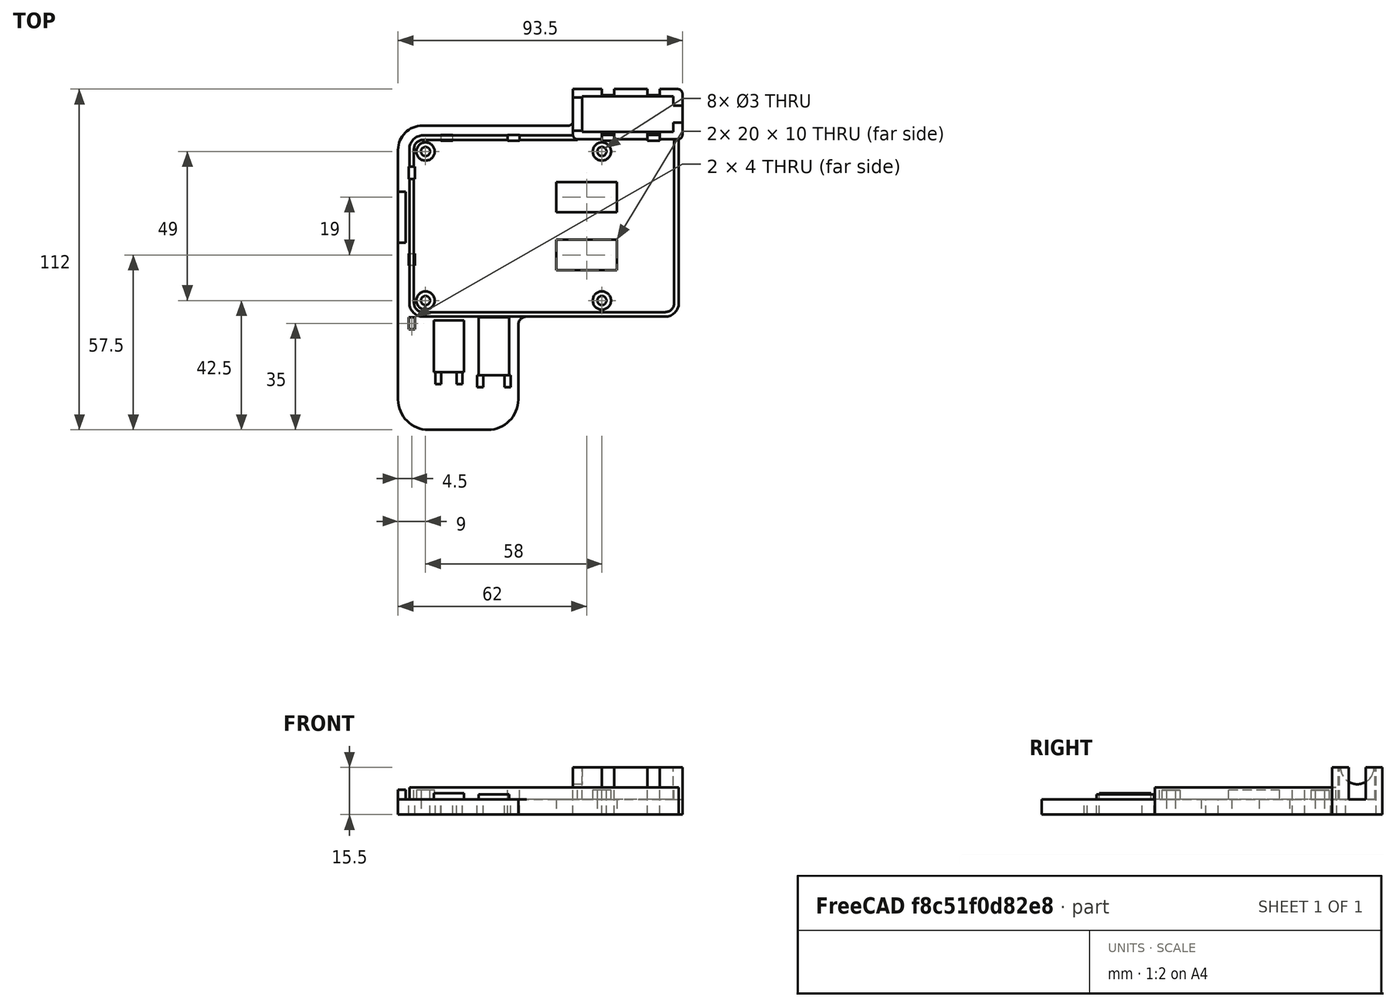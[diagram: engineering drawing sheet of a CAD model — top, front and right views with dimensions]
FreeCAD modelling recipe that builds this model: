
FCSTD DOCUMENT  (FreeCAD 0.18R4 (GitTag))
Label: v1.1raspberry_holster
License: All rights reserved
LicenseURL: http://en.wikipedia.org/wiki/All_rights_reserved
objects: Sketcher::SketchObject×10, PartDesign::Pad×7, PartDesign::Pocket×3, Mesh::Feature×1, PartDesign::Body×1
note: 31 computed .brp shape members not serialized (recipe doc carries the construction recipe); baked Part::Feature solids carry a one-line shape summary decoded from their .brp

FEATURE [Mesh::Feature] Raspberry_Pi_4
  Placement = pos=(39,24.5,7.5) rot=(0,0,1;0rad)
FEATURE [Sketcher::SketchObject] Sketch  label="bottom_plane"
  MapMode = 5
  Support = -> [XY_Plane]
  sketch-geometry (71):
    g0: Circle CenterX=0 CenterY=49 CenterZ=0 NormalX=0 NormalY=0 NormalZ=1 AngleXU=0 Radius=1.5
    g1: Circle CenterX=58 CenterY=49 CenterZ=0 NormalX=0 NormalY=0 NormalZ=1 AngleXU=0 Radius=1.5
    g2: Circle CenterX=0 CenterY=0 CenterZ=0 NormalX=0 NormalY=0 NormalZ=1 AngleXU=0 Radius=1.5
    g3: Circle CenterX=58 CenterY=0 CenterZ=0 NormalX=0 NormalY=0 NormalZ=1 AngleXU=0 Radius=1.5
    g4: LineSegment StartX=84.5 StartY=68 StartZ=0 EndX=84.5 EndY=-5 EndZ=0
    g5: ArcOfCircle CenterX=83 CenterY=68 CenterZ=0 NormalX=0 NormalY=0 NormalZ=1 AngleXU=0 Radius=1.5 StartAngle=-9e-16 EndAngle=1.5708
    g6: LineSegment StartX=48.5 StartY=69.5 StartZ=0 EndX=48.5 EndY=59 EndZ=0
    g7: ArcOfCircle CenterX=47 CenterY=59 CenterZ=0 NormalX=0 NormalY=0 NormalZ=1 AngleXU=0 Radius=1.5 StartAngle=4.71239 EndAngle=6.28319
    g8: LineSegment StartX=47 StartY=57.5 StartZ=0 EndX=-1 EndY=57.5 EndZ=0
    g9: LineSegment StartX=-9 StartY=49.5 StartZ=0 EndX=-9 EndY=-32.5 EndZ=0
    g10: ArcOfCircle CenterX=-1 CenterY=49.5 CenterZ=0 NormalX=0 NormalY=0 NormalZ=1 AngleXU=0 Radius=8 StartAngle=1.5708 EndAngle=3.14159
    g11: LineSegment StartX=1 StartY=-42.5 StartZ=0 EndX=20.5 EndY=-42.5 EndZ=0
    g12: ArcOfCircle CenterX=1 CenterY=-32.5 CenterZ=0 NormalX=0 NormalY=0 NormalZ=1 AngleXU=0 Radius=10 StartAngle=3.14159 EndAngle=4.71239
    g13: ArcOfCircle CenterX=83 CenterY=-5 CenterZ=0 NormalX=0 NormalY=0 NormalZ=1 AngleXU=0 Radius=1.5 StartAngle=4.71239 EndAngle=6.28319
    g14: LineSegment StartX=32 StartY=-6.5 StartZ=0 EndX=83 EndY=-6.5 EndZ=0
    g15: LineSegment StartX=30.5 StartY=-8 StartZ=0 EndX=30.5 EndY=-32.5 EndZ=0
    g16: ArcOfCircle CenterX=32 CenterY=-8 CenterZ=0 NormalX=0 NormalY=0 NormalZ=1 AngleXU=0 Radius=1.5 StartAngle=1.5708 EndAngle=3.14159
    g17: ArcOfCircle CenterX=20.5 CenterY=-32.5 CenterZ=0 NormalX=0 NormalY=0 NormalZ=1 AngleXU=0 Radius=10 StartAngle=4.71239 EndAngle=6.28319
    g18: LineSegment StartX=58 StartY=52.5 StartZ=0 EndX=62 EndY=52.5 EndZ=0
    g19: LineSegment StartX=62 StartY=52.5 StartZ=0 EndX=62 EndY=54.5 EndZ=0
    g20: LineSegment StartX=62 StartY=54.5 StartZ=0 EndX=58 EndY=54.5 EndZ=0
    g21: LineSegment StartX=58 StartY=54.5 StartZ=0 EndX=58 EndY=52.5 EndZ=0
    g22: LineSegment StartX=73 StartY=54.5 StartZ=0 EndX=77 EndY=54.5 EndZ=0
    g23: LineSegment StartX=77 StartY=54.5 StartZ=0 EndX=77 EndY=52.5 EndZ=0
    g24: LineSegment StartX=77 StartY=52.5 StartZ=0 EndX=73 EndY=52.5 EndZ=0
    g25: LineSegment StartX=73 StartY=52.5 StartZ=0 EndX=73 EndY=54.5 EndZ=0
    g26: LineSegment StartX=48.5 StartY=69.5 StartZ=0 EndX=58 EndY=69.5 EndZ=0
    g27: LineSegment StartX=58 StartY=69.5 StartZ=0 EndX=58 EndY=67.5 EndZ=0
    g28: LineSegment StartX=58 StartY=67.5 StartZ=0 EndX=62 EndY=67.5 EndZ=0
    g29: LineSegment StartX=62 StartY=67.5 StartZ=0 EndX=62 EndY=69.5 EndZ=0
    g30: LineSegment StartX=62 StartY=69.5 StartZ=0 EndX=73 EndY=69.5 EndZ=0
    g31: LineSegment StartX=73 StartY=69.5 StartZ=0 EndX=73 EndY=67.5 EndZ=0
    g32: LineSegment StartX=73 StartY=67.5 StartZ=0 EndX=77 EndY=67.5 EndZ=0
    g33: LineSegment StartX=77 StartY=67.5 StartZ=0 EndX=77 EndY=69.5 EndZ=0
    g34: LineSegment StartX=77 StartY=69.5 StartZ=0 EndX=83 EndY=69.5 EndZ=0
    g35: LineSegment StartX=31 StartY=54.5 StartZ=0 EndX=27 EndY=54.5 EndZ=0
    g36: LineSegment StartX=27 StartY=54.5 StartZ=0 EndX=27 EndY=52.5 EndZ=0
    g37: LineSegment StartX=27 StartY=52.5 StartZ=0 EndX=31 EndY=52.5 EndZ=0
    g38: LineSegment StartX=31 StartY=52.5 StartZ=0 EndX=31 EndY=54.5 EndZ=0
    g39: LineSegment StartX=9 StartY=54.5 StartZ=0 EndX=5 EndY=54.5 EndZ=0
    g40: LineSegment StartX=5 StartY=54.5 StartZ=0 EndX=5 EndY=52.5 EndZ=0
    g41: LineSegment StartX=5 StartY=52.5 StartZ=0 EndX=9 EndY=52.5 EndZ=0
    g42: LineSegment StartX=9 StartY=52.5 StartZ=0 EndX=9 EndY=54.5 EndZ=0
    g43: LineSegment StartX=-5.5 StartY=44 StartZ=0 EndX=-3.5 EndY=44 EndZ=0
    g44: LineSegment StartX=-3.5 StartY=44 StartZ=0 EndX=-3.5 EndY=40 EndZ=0
    g45: LineSegment StartX=-3.5 StartY=40 StartZ=0 EndX=-5.5 EndY=40 EndZ=0
    g46: LineSegment StartX=-5.5 StartY=40 StartZ=0 EndX=-5.5 EndY=44 EndZ=0
    g47: LineSegment StartX=-5.5 StartY=15.5 StartZ=0 EndX=-3.5 EndY=15.5 EndZ=0
    g48: LineSegment StartX=-3.5 StartY=15.5 StartZ=0 EndX=-3.5 EndY=11.5 EndZ=0
    g49: LineSegment StartX=-3.5 StartY=11.5 StartZ=0 EndX=-5.5 EndY=11.5 EndZ=0
    g50: LineSegment StartX=-5.5 StartY=11.5 StartZ=0 EndX=-5.5 EndY=15.5 EndZ=0
    g51: LineSegment StartX=-5.5 StartY=-5.5 StartZ=0 EndX=-3.5 EndY=-5.5 EndZ=0
    g52: LineSegment StartX=-3.5 StartY=-5.5 StartZ=0 EndX=-3.5 EndY=-9.5 EndZ=0
    g53: LineSegment StartX=-3.5 StartY=-9.5 StartZ=0 EndX=-5.5 EndY=-9.5 EndZ=0
    g54: LineSegment StartX=-5.5 StartY=-9.5 StartZ=0 EndX=-5.5 EndY=-5.5 EndZ=0
    g55: LineSegment StartX=3.2 StartY=-23.5 StartZ=0 EndX=5.2 EndY=-23.5 EndZ=0
    g56: LineSegment StartX=5.2 StartY=-23.5 StartZ=0 EndX=5.2 EndY=-27.5 EndZ=0
    g57: LineSegment StartX=5.2 StartY=-27.5 StartZ=0 EndX=3.2 EndY=-27.5 EndZ=0
    g58: LineSegment StartX=3.2 StartY=-27.5 StartZ=0 EndX=3.2 EndY=-23.5 EndZ=0
    g59: LineSegment StartX=10.2 StartY=-23.5 StartZ=0 EndX=12.2 EndY=-23.5 EndZ=0
    g60: LineSegment StartX=12.2 StartY=-23.5 StartZ=0 EndX=12.2 EndY=-27.5 EndZ=0
    g61: LineSegment StartX=12.2 StartY=-27.5 StartZ=0 EndX=10.2 EndY=-27.5 EndZ=0
    g62: LineSegment StartX=10.2 StartY=-27.5 StartZ=0 EndX=10.2 EndY=-23.5 EndZ=0
    g63: LineSegment StartX=17 StartY=-24.5 StartZ=0 EndX=19 EndY=-24.5 EndZ=0
    g64: LineSegment StartX=19 StartY=-24.5 StartZ=0 EndX=19 EndY=-28.5 EndZ=0
    g65: LineSegment StartX=19 StartY=-28.5 StartZ=0 EndX=17 EndY=-28.5 EndZ=0
    g66: LineSegment StartX=17 StartY=-28.5 StartZ=0 EndX=17 EndY=-24.5 EndZ=0
    g67: LineSegment StartX=26 StartY=-24.5 StartZ=0 EndX=28 EndY=-24.5 EndZ=0
    g68: LineSegment StartX=28 StartY=-24.5 StartZ=0 EndX=28 EndY=-28.5 EndZ=0
    g69: LineSegment StartX=28 StartY=-28.5 StartZ=0 EndX=26 EndY=-28.5 EndZ=0
    g70: LineSegment StartX=26 StartY=-28.5 StartZ=0 EndX=26 EndY=-24.5 EndZ=0
  constraints (219):
    c: Coincident(g-1,g2)
    c: Vertical(g2,g0)
    c: Vertical(g1,g3)
    c: Horizontal(g1,g0)
    c: Horizontal(g3,g2)
    c: DistanceY(g2,g0) = 49
    c: DistanceX(g2,g3) = 58
    c: Radius(g2) = 1.5
    c: Equal(g2,g3)
    c: Equal(g3,g1)
    c: Equal(g1,g0)
    c: Vertical(g4)
    c: DistanceX(g3,g4) = 26.5
    c: Coincident(g5,g4)
    c: Vertical(g5,g5)
    c: Horizontal(g4,g5)
    c: Radius(g5) = 1.5
    c: Coincident(g6,g7)
    c: Vertical(g7,g7)
    c: Horizontal(g7,g6)
    c: Radius(g7) = 1.5
    c: Vertical(g6)
    c: DistanceX(g6,g4) = 36
    c: Coincident(g8,g7)
    c: Horizontal(g8)
    c: Vertical(g9)
    c: DistanceX(g9,g0) = 9
    c: DistanceY(g1,g7) = 8.5
    c: Coincident(g10,g8)
    c: Coincident(g9,g10)
    c: Vertical(g10,g8)
    c: Horizontal(g10,g9)
    c: Horizontal(g11)
    c: DistanceY(g11,g2) = 42.5
    c: Coincident(g11,g12)
    c: Coincident(g12,g9)
    c: Vertical(g12,g11)
    c: Horizontal(g9,g12)
    c: Coincident(g13,g4)
    c: Horizontal(g13,g4)
    c: Vertical(g13,g13)
    c: Radius(g13) = 1.5
    c: Coincident(g14,g13)
    c: Horizontal(g14)
    c: Coincident(g16,g14)
    c: Coincident(g16,g15)
    c: Vertical(g16,g14)
    c: Horizontal(g16,g15)
    c: DistanceY(g14,g3) = 6.5
    c: DistanceX(g2,g15) = 30.5
    c: Vertical(g15)
    c: Coincident(g17,g11)
    c: Coincident(g17,g15)
    c: Horizontal(g17,g15)
    c: Vertical(g11,g17)
    c: Radius(g16) = 1.5
    c: Coincident(g18,g19)
    c: Coincident(g19,g20)
    c: Coincident(g20,g21)
    c: Coincident(g21,g18)
    c: Horizontal(g18)
    c: Horizontal(g20)
    c: Vertical(g19)
    c: Vertical(g21)
    c: DistanceY(g18,g20) = 2
    c: DistanceX(g20,g19) = 4
    c: DistanceY(g1,g18) = 3.5
    c: Vertical(g1,g18)
    c: Coincident(g22,g23)
    c: Coincident(g23,g24)
    c: Coincident(g24,g25)
    c: Coincident(g25,g22)
    c: Horizontal(g22)
    c: Horizontal(g24)
    c: Vertical(g23)
    c: Vertical(g25)
    c: Horizontal(g22,g19)
    c: Horizontal(g24,g18)
    c: DistanceX(g22,g22) = 4
    c: DistanceX(g18,g24) = 15
    c: Coincident(g26,g27)
    c: Coincident(g27,g28)
    c: Coincident(g28,g29)
    c: Coincident(g29,g30)
    c: Coincident(g30,g31)
    c: Coincident(g31,g32)
    c: Coincident(g32,g33)
    c: Coincident(g33,g34)
    c: Coincident(g26,g6)
    c: Coincident(g34,g5)
    c: DistanceY(g1,g6) = 20.5
    c: Horizontal(g26)
    c: Horizontal(g30)
    c: Horizontal(g32)
    c: Horizontal(g34)
    c: Horizontal(g28)
    c: Vertical(g27)
    c: Vertical(g29)
    c: Vertical(g31)
    c: Vertical(g33)
    c: Horizontal(g26,g29)
    c: Horizontal(g30,g33)
    c: Horizontal(g31,g28)
    c: Vertical(g28,g19)
    c: Vertical(g20,g27)
    c: Vertical(g22,g31)
    c: Vertical(g22,g32)
    c: DistanceY(g28,g29) = 2
    c: Coincident(g35,g36)
    c: Coincident(g36,g37)
    c: Coincident(g38,g35)
    c: Horizontal(g35)
    c: Horizontal(g37)
    c: Vertical(g36)
    c: Vertical(g38)
    c: Coincident(g39,g40)
    c: Coincident(g40,g41)
    c: Coincident(g41,g42)
    c: Coincident(g42,g39)
    c: Horizontal(g39)
    c: Horizontal(g41)
    c: Vertical(g40)
    c: Vertical(g42)
    c: Coincident(g43,g44)
    c: Coincident(g44,g45)
    c: Coincident(g45,g46)
    c: Coincident(g46,g43)
    c: Horizontal(g43)
    c: Horizontal(g45)
    c: Vertical(g44)
    c: Vertical(g46)
    c: Coincident(g47,g48)
    c: Coincident(g48,g49)
    c: Coincident(g49,g50)
    c: Coincident(g50,g47)
    c: Horizontal(g47)
    c: Horizontal(g49)
    c: Vertical(g48)
    c: Vertical(g50)
    c: DistanceY(g1,g37) = 3.5
    c: DistanceX(g36,g37) = 4
    c: DistanceY(g37,g35) = 2
    c: DistanceX(g40,g41) = 4
    c: Horizontal(g41,g36)
    c: Horizontal(g39,g35)
    c: DistanceX(g37,g1) = 27
    c: DistanceX(g43,g0) = 3.5
    c: DistanceX(g43,g43) = 2
    c: DistanceY(g44,g43) = 4
    c: Vertical(g44,g47)
    c: Vertical(g47,g45)
    c: DistanceY(g49,g47) = 4
    c: DistanceY(g43,g0) = 5
    c: DistanceX(g0,g40) = 5
    c: DistanceY(g47,g44) = 24.5
    c: Coincident(g37,g38)
    c: Coincident(g51,g52)
    c: Coincident(g52,g53)
    c: Coincident(g53,g54)
    c: Coincident(g54,g51)
    c: Horizontal(g51)
    c: Horizontal(g53)
    c: Vertical(g52)
    c: Vertical(g54)
    c: Vertical(g51,g49)
    c: Vertical(g51,g48)
    c: DistanceY(g53,g51) = 4
    c: DistanceY(g51,g48) = 17
    c: Coincident(g55,g56)
    c: Coincident(g56,g57)
    c: Coincident(g57,g58)
    c: Coincident(g58,g55)
    c: Horizontal(g55)
    c: Horizontal(g57)
    c: Vertical(g56)
    c: Vertical(g58)
    c: Coincident(g59,g60)
    c: Coincident(g60,g61)
    c: Coincident(g61,g62)
    c: Coincident(g62,g59)
    c: Horizontal(g59)
    c: Horizontal(g61)
    c: Vertical(g60)
    c: Vertical(g62)
    c: Coincident(g63,g64)
    c: Coincident(g64,g65)
    c: Coincident(g65,g66)
    c: Coincident(g66,g63)
    c: Horizontal(g63)
    c: Horizontal(g65)
    c: Vertical(g64)
    c: Vertical(g66)
    c: Coincident(g67,g68)
    c: Coincident(g68,g69)
    c: Coincident(g69,g70)
    c: Coincident(g70,g67)
    c: Horizontal(g67)
    c: Horizontal(g69)
    c: Vertical(g68)
    c: Vertical(g70)
    c: DistanceX(g55,g55) = 2
    c: DistanceY(g56,g55) = 4
    c: Horizontal(g56,g61)
    c: Horizontal(g65,g69)
    c: Horizontal(g67,g63)
    c: Horizontal(g59,g55)
    c: DistanceX(g59,g59) = 2
    c: DistanceX(g63,g63) = 2
    c: DistanceX(g67,g67) = 2
    c: DistanceX(g56,g61) = 5
    c: DistanceX(g64,g69) = 7
    c: DistanceY(g65,g63) = 4
    c: DistanceY(g55,g2) = 23.5
    c: DistanceY(g63,g2) = 24.5
    c: DistanceX(g2,g55) = 5.2
    c: DistanceX(g2,g63) = 19
    c: Radius(g10) = 8
    c: Equal(g12,g17)
    c: Radius(g17) = 10
FEATURE [PartDesign::Pad] Pad  label="bottom_plane_pad"
  Length = 5
  Length2 = 100
  Profile = -> Sketch
  Type = 0
FEATURE [Sketcher::SketchObject] Sketch001  label="standoffs"
  ExternalGeometry = -> [Pad]
  MapMode = 5
  Placement = pos=(0,0,5) rot=(0,0,1;0rad)
  Support = -> [Pad]
  sketch-geometry (8):
    g0: Circle CenterX=0 CenterY=49 CenterZ=0 NormalX=0 NormalY=0 NormalZ=1 AngleXU=0 Radius=3
    g1: Circle CenterX=58 CenterY=49 CenterZ=0 NormalX=0 NormalY=0 NormalZ=1 AngleXU=0 Radius=3
    g2: Circle CenterX=58 CenterY=0 CenterZ=0 NormalX=0 NormalY=0 NormalZ=1 AngleXU=0 Radius=3
    g3: Circle CenterX=0 CenterY=0 CenterZ=0 NormalX=0 NormalY=0 NormalZ=1 AngleXU=0 Radius=3
    g4: Circle CenterX=58 CenterY=0 CenterZ=0 NormalX=0 NormalY=0 NormalZ=1 AngleXU=0 Radius=1.5
    g5: Circle CenterX=58 CenterY=49 CenterZ=0 NormalX=0 NormalY=0 NormalZ=1 AngleXU=0 Radius=1.5
    g6: Circle CenterX=0 CenterY=49 CenterZ=0 NormalX=0 NormalY=0 NormalZ=1 AngleXU=0 Radius=1.5
    g7: Circle CenterX=0 CenterY=0 CenterZ=0 NormalX=0 NormalY=0 NormalZ=1 AngleXU=0 Radius=1.5
  constraints (16):
    c: Coincident(g3,g-1)
    c: Coincident(g-5,g0)
    c: Coincident(g-6,g1)
    c: Coincident(g-3,g2)
    c: Equal(g2,g1)
    c: Equal(g1,g0)
    c: Equal(g0,g3)
    c: Radius(g1) = 3
    c: Coincident(g7,g3)
    c: Coincident(g2,g4)
    c: Coincident(g5,g1)
    c: Coincident(g6,g0)
    c: Equal(g5,g4)
    c: Equal(g4,g7)
    c: Equal(g7,g6)
    c: Equal(g6,g-5)
FEATURE [PartDesign::Pad] Pad001  label="standoffs_pad"
  BaseFeature = -> Pad
  Length = 3
  Length2 = 100
  Profile = -> Sketch001
  Type = 0
FEATURE [Sketcher::SketchObject] Sketch002  label="HDMI_holder"
  ExternalGeometry = -> [Pad001]
  MapMode = 5
  Placement = pos=(0,0,5) rot=(0,0,1;0rad)
  Support = -> [Pad001]
  sketch-geometry (31):
    g0: LineSegment StartX=84.5 StartY=54.5 StartZ=0 EndX=84.5 EndY=58.5 EndZ=0
    g1: LineSegment StartX=51.5 StartY=55.5 StartZ=0 EndX=81.5 EndY=55.5 EndZ=0
    g2: LineSegment StartX=81.5 StartY=55.5 StartZ=0 EndX=81.5 EndY=58.5 EndZ=0
    g3: LineSegment StartX=81.5 StartY=58.5 StartZ=0 EndX=84.5 EndY=58.5 EndZ=0
    g4: LineSegment StartX=51.5 StartY=55.5 StartZ=0 EndX=51.5 EndY=67.1 EndZ=0
    g5: LineSegment StartX=48.5 StartY=69.5 StartZ=0 EndX=48.5 EndY=54.5 EndZ=0
    g6: LineSegment StartX=51.5 StartY=67.1 StartZ=0 EndX=81.5 EndY=67.1 EndZ=0
    g7: LineSegment StartX=81.5 StartY=67.1 StartZ=0 EndX=81.5 EndY=64.1 EndZ=0
    g8: LineSegment StartX=81.5 StartY=64.1 StartZ=0 EndX=84.5 EndY=64.1 EndZ=0
    g9: LineSegment StartX=84.5 StartY=64.1 StartZ=0 EndX=84.5 EndY=68 EndZ=0
    g10: ArcOfCircle CenterX=83 CenterY=68 CenterZ=0 NormalX=0 NormalY=0 NormalZ=1 AngleXU=0 Radius=1.5 StartAngle=1.4e-15 EndAngle=1.5708
    g11: LineSegment StartX=83 StartY=69.5 StartZ=0 EndX=77 EndY=69.5 EndZ=0
    g12: LineSegment StartX=77 StartY=69.5 StartZ=0 EndX=77 EndY=67.5 EndZ=0
    g13: LineSegment StartX=77 StartY=67.5 StartZ=0 EndX=73 EndY=67.5 EndZ=0
    g14: LineSegment StartX=73 StartY=67.5 StartZ=0 EndX=73 EndY=69.5 EndZ=0
    g15: LineSegment StartX=73 StartY=69.5 StartZ=0 EndX=62 EndY=69.5 EndZ=0
    g16: LineSegment StartX=62 StartY=69.5 StartZ=0 EndX=62 EndY=67.5 EndZ=0
    g17: LineSegment StartX=62 StartY=67.5 StartZ=0 EndX=58 EndY=67.5 EndZ=0
    g18: LineSegment StartX=58 StartY=67.5 StartZ=0 EndX=58 EndY=69.5 EndZ=0
    g19: LineSegment StartX=58 StartY=69.5 StartZ=0 EndX=48.5 EndY=69.5 EndZ=0
    g20: ArcOfCircle CenterX=50 CenterY=54.5 CenterZ=0 NormalX=0 NormalY=0 NormalZ=1 AngleXU=0 Radius=1.5 StartAngle=3.14159 EndAngle=4.71239
    g21: LineSegment StartX=83 StartY=53 StartZ=0 EndX=77 EndY=53 EndZ=0
    g22: LineSegment StartX=77 StartY=53 StartZ=0 EndX=77 EndY=55 EndZ=0
    g23: LineSegment StartX=77 StartY=55 StartZ=0 EndX=73 EndY=55 EndZ=0
    g24: LineSegment StartX=73 StartY=55 StartZ=0 EndX=73 EndY=53 EndZ=0
    g25: LineSegment StartX=73 StartY=53 StartZ=0 EndX=62 EndY=53 EndZ=0
    g26: LineSegment StartX=62 StartY=53 StartZ=0 EndX=62 EndY=55 EndZ=0
    g27: LineSegment StartX=62 StartY=55 StartZ=0 EndX=58 EndY=55 EndZ=0
    g28: LineSegment StartX=58 StartY=53 StartZ=0 EndX=50 EndY=53 EndZ=0
    g29: ArcOfCircle CenterX=83 CenterY=54.5 CenterZ=0 NormalX=0 NormalY=0 NormalZ=1 AngleXU=0 Radius=1.5 StartAngle=4.71239 EndAngle=6.28319
    g30: LineSegment StartX=58 StartY=53 StartZ=0 EndX=58 EndY=55 EndZ=0
  constraints (89):
    c: Vertical(g0,g-6)
    c: Horizontal(g1)
    c: DistanceY(g20,g1) = 2.5
    c: Coincident(g0,g3)
    c: Coincident(g3,g2)
    c: Coincident(g2,g1)
    c: DistanceX(g2,g0) = 3
    c: Vertical(g0)
    c: Horizontal(g3)
    c: Vertical(g2)
    c: DistanceX(g1,g1) = 30
    c: DistanceY(g1,g2) = 3
    c: Coincident(g4,g6)
    c: Coincident(g1,g4)
    c: Coincident(g8,g9)
    c: Coincident(g7,g8)
    c: Coincident(g6,g7)
    c: Horizontal(g6)
    c: Vertical(g4)
    c: DistanceY(g1,g4) = 11.6
    c: Vertical(g7)
    c: Horizontal(g8)
    c: Vertical(g9)
    c: Vertical(g7,g2)
    c: DistanceY(g7,g6) = 3
    c: Coincident(g9,g-6)
    c: Coincident(g9,g10)
    c: Horizontal(g9,g10)
    c: Vertical(g10,g10)
    c: Radius(g10) = 1.5
    c: Coincident(g11,g12)
    c: Coincident(g12,g13)
    c: Coincident(g13,g14)
    c: Coincident(g14,g15)
    c: Coincident(g15,g16)
    c: Coincident(g16,g17)
    c: Coincident(g17,g18)
    c: Coincident(g18,g19)
    c: Coincident(g11,g10)
    c: Horizontal(g11)
    c: Vertical(g12)
    c: Coincident(g12,g-4)
    c: Coincident(g13,g-4)
    c: Coincident(g14,g-7)
    c: Coincident(g15,g-7)
    c: Coincident(g16,g-5)
    c: Coincident(g17,g-5)
    c: Coincident(g19,g-8)
    c: Horizontal(g19)
    c: Vertical(g18)
    c: Coincident(g5,g19)
    c: Coincident(g5,g20)
    c: Horizontal(g20,g5)
    c: Vertical(g20,g20)
    c: Radius(g20) = 1.5
    c: Vertical(g5)
    c: Coincident(g21,g22)
    c: Coincident(g22,g23)
    c: Coincident(g23,g24)
    c: Coincident(g24,g25)
    c: Coincident(g25,g26)
    c: Coincident(g26,g27)
    c: Coincident(g20,g28)
    c: Coincident(g23,g-9)
    c: Coincident(g29,g0)
    c: Coincident(g21,g29)
    c: Vertical(g29,g21)
    c: Horizontal(g29,g0)
    c: Radius(g29) = 1.5
    c: DistanceY(g-3,g28) = 4
    c: Horizontal(g28)
    c: Horizontal(g25)
    c: Horizontal(g21)
    c: Horizontal(g21,g24)
    c: Horizontal(g25,g28)
    c: Coincident(g30,g27)
    c: Coincident(g28,g30)
    c: Vertical(g27,g17)
    c: Vertical(g26,g16)
    c: Vertical(g22,g12)
    c: Vertical(g23,g13)
    c: Horizontal(g23)
    c: Horizontal(g27)
    c: Horizontal(g26,g23)
    c: Vertical(g26)
    c: Vertical(g24)
    c: Vertical(g22)
    c: Vertical(g30)
    c: DistanceY(g28,g27) = 2
FEATURE [PartDesign::Pad] Pad002  label="HDMI_holder_pad"
  BaseFeature = -> Pad001
  Length = 10.5
  Length2 = 100
  Profile = -> Sketch002
  Type = 0
FEATURE [Sketcher::SketchObject] Sketch003  label="HDMI_wire_hole"
  ExternalGeometry = -> [Pad002]
  MapMode = 5
  Placement = pos=(48.5,0,0) rot=(0.57735,-0.57735,-0.57735;2.0944rad)
  Support = -> [Pad002]
  sketch-geometry (1):
    g0: Circle CenterX=-61.3 CenterY=15.5 CenterZ=0 NormalX=0 NormalY=0 NormalZ=1 AngleXU=0 Radius=5.5
  constraints (1):
    c: Radius(g0) = 5.5
FEATURE [PartDesign::Pocket] Pocket  label="Pocket_HDMI_wire_hole"
  BaseFeature = -> Pad002
  Length = 5
  Length2 = 100
  Profile = -> Sketch003
  Type = 0
FEATURE [Sketcher::SketchObject] Sketch004  label="SDcard_holder"
  ExternalGeometry = -> [Pocket]
  MapMode = 5
  Placement = pos=(0,0,5) rot=(0,0,1;0rad)
  Support = -> [Pocket]
  sketch-geometry (4):
    g0: LineSegment StartX=-9 StartY=35.8003 StartZ=0 EndX=-6.5 EndY=35.8003 EndZ=0
    g1: LineSegment StartX=-6.5 StartY=35.8003 StartZ=0 EndX=-6.5 EndY=19 EndZ=0
    g2: LineSegment StartX=-6.5 StartY=19 StartZ=0 EndX=-9 EndY=19 EndZ=0
    g3: LineSegment StartX=-9 StartY=19 StartZ=0 EndX=-9 EndY=35.8003 EndZ=0
  constraints (12):
    c: Coincident(g0,g1)
    c: Coincident(g1,g2)
    c: Coincident(g2,g3)
    c: Coincident(g3,g0)
    c: Horizontal(g0)
    c: Horizontal(g2)
    c: Vertical(g1)
    c: Vertical(g3)
    c: DistanceY(g-1,g1) = 19
    c: DistanceY(g0,g-4) = 19
    c: Vertical(g0,g-5)
    c: DistanceX(g1,g-1) = 6.5
FEATURE [PartDesign::Pad] Pad003  label="SDcard_holder_pad"
  BaseFeature = -> Pocket
  Length = 3.2
  Length2 = 100
  Profile = -> Sketch004
  Type = 0
FEATURE [Sketcher::SketchObject] Sketch005  label="typeC_support"
  ExternalGeometry = -> [Pad003]
  MapMode = 5
  Placement = pos=(0,0,5) rot=(0,0,1;0rad)
  Support = -> [Pad003]
  sketch-geometry (4):
    g0: LineSegment StartX=2.7 StartY=-6.5 StartZ=0 EndX=12.7 EndY=-6.5 EndZ=0
    g1: LineSegment StartX=12.7 StartY=-6.5 StartZ=0 EndX=12.7 EndY=-23.5 EndZ=0
    g2: LineSegment StartX=12.7 StartY=-23.5 StartZ=0 EndX=2.7 EndY=-23.5 EndZ=0
    g3: LineSegment StartX=2.7 StartY=-23.5 StartZ=0 EndX=2.7 EndY=-6.5 EndZ=0
  constraints (12):
    c: Coincident(g0,g1)
    c: Coincident(g1,g2)
    c: Coincident(g2,g3)
    c: Coincident(g3,g0)
    c: Horizontal(g0)
    c: Horizontal(g2)
    c: Vertical(g1)
    c: Vertical(g3)
    c: DistanceX(g0,g0) = 10
    c: DistanceY(g1,g1) = 17
    c: Horizontal(g2,g-4)
    c: DistanceX(g-1,g0) = 2.7
FEATURE [PartDesign::Pad] Pad004  label="typeC_support_pad"
  BaseFeature = -> Pad003
  Length = 2
  Length2 = 100
  Profile = -> Sketch005
  Type = 0
FEATURE [Sketcher::SketchObject] Sketch006  label="microHDMI_support"
  ExternalGeometry = -> [Pad004]
  MapMode = 5
  Placement = pos=(0,0,5) rot=(0,0,1;0rad)
  Support = -> [Pad004]
  sketch-geometry (4):
    g0: LineSegment StartX=17.5 StartY=-5.5 StartZ=0 EndX=27.5 EndY=-5.5 EndZ=0
    g1: LineSegment StartX=27.5 StartY=-5.5 StartZ=0 EndX=27.5 EndY=-24.5 EndZ=0
    g2: LineSegment StartX=27.5 StartY=-24.5 StartZ=0 EndX=17.5 EndY=-24.5 EndZ=0
    g3: LineSegment StartX=17.5 StartY=-24.5 StartZ=0 EndX=17.5 EndY=-5.5 EndZ=0
  constraints (12):
    c: Coincident(g0,g1)
    c: Coincident(g1,g2)
    c: Coincident(g2,g3)
    c: Coincident(g3,g0)
    c: Horizontal(g0)
    c: Horizontal(g2)
    c: Vertical(g1)
    c: Vertical(g3)
    c: DistanceX(g0,g0) = 10
    c: DistanceY(g1,g1) = 19
    c: Horizontal(g2,g-4)
    c: DistanceX(g-1,g0) = 17.5
FEATURE [PartDesign::Pad] Pad005  label="microHDMI_support_pad"
  BaseFeature = -> Pad004
  Length = 1.7
  Length2 = 100
  Profile = -> Sketch006
  Type = 0
FEATURE [Sketcher::SketchObject] Sketch007  label="dust_cover"
  ExternalGeometry = -> [Pad005]
  MapMode = 5
  Placement = pos=(0,0,5) rot=(0,0,1;0rad)
  Support = -> [Pad005]
  sketch-geometry (26):
    g0: LineSegment StartX=81.8 StartY=53 StartZ=0 EndX=81.8 EndY=-0.8 EndZ=0
    g1: LineSegment StartX=78.8 StartY=-3.8 StartZ=0 EndX=-0.8 EndY=-3.8 EndZ=0
    g2: LineSegment StartX=-3.8 StartY=49.8 StartZ=0 EndX=-3.8 EndY=44 EndZ=0
    g3: LineSegment StartX=-3.8 StartY=40 StartZ=0 EndX=-3.8 EndY=-0.8 EndZ=0
    g4: LineSegment StartX=-3.8 StartY=40 StartZ=0 EndX=-5.3 EndY=40 EndZ=0
    g5: ArcOfCircle CenterX=-0.8 CenterY=-0.8 CenterZ=0 NormalX=0 NormalY=0 NormalZ=1 AngleXU=0 Radius=3 StartAngle=3.14159 EndAngle=4.71239
    g6: ArcOfCircle CenterX=78.8 CenterY=-0.8 CenterZ=0 NormalX=0 NormalY=0 NormalZ=1 AngleXU=0 Radius=3 StartAngle=4.71239 EndAngle=6.28319
    g7: LineSegment StartX=81.8 StartY=53 StartZ=0 EndX=83 EndY=53 EndZ=0
    g8: LineSegment StartX=83.3 StartY=53.0303 StartZ=0 EndX=83.3 EndY=-0.8 EndZ=0
    g9: ArcOfCircle CenterX=83 CenterY=54.5 CenterZ=0 NormalX=0 NormalY=0 NormalZ=1 AngleXU=0 Radius=1.5 StartAngle=4.71239 EndAngle=4.91375
    g10: ArcOfCircle CenterX=78.8 CenterY=-0.8 CenterZ=0 NormalX=0 NormalY=0 NormalZ=1 AngleXU=0 Radius=4.5 StartAngle=4.71239 EndAngle=6.28319
    g11: LineSegment StartX=-0.8 StartY=-5.3 StartZ=0 EndX=78.8 EndY=-5.3 EndZ=0
    g12: ArcOfCircle CenterX=-0.8 CenterY=-0.8 CenterZ=0 NormalX=0 NormalY=0 NormalZ=1 AngleXU=0 Radius=4.5 StartAngle=3.14159 EndAngle=4.71239
    g13: LineSegment StartX=-5.3 StartY=-0.8 StartZ=0 EndX=-5.3 EndY=40 EndZ=0
    g14: LineSegment StartX=27 StartY=54.3 StartZ=0 EndX=27 EndY=52.8 EndZ=0
    g15: LineSegment StartX=27 StartY=54.3 StartZ=0 EndX=-0.8 EndY=54.3 EndZ=0
    g16: ArcOfCircle CenterX=-0.8 CenterY=49.8 CenterZ=0 NormalX=0 NormalY=0 NormalZ=1 AngleXU=0 Radius=4.5 StartAngle=1.5708 EndAngle=3.14159
    g17: LineSegment StartX=-3.8 StartY=44 StartZ=0 EndX=-5.3 EndY=44 EndZ=0
    g18: LineSegment StartX=-5.3 StartY=49.8 StartZ=0 EndX=-5.3 EndY=44 EndZ=0
    g19: LineSegment StartX=31 StartY=54.3 StartZ=0 EndX=48.5134 EndY=54.3 EndZ=0
    g20: LineSegment StartX=50 StartY=52.8 StartZ=0 EndX=31 EndY=52.8 EndZ=0
    g21: LineSegment StartX=31 StartY=52.8 StartZ=0 EndX=31 EndY=54.3 EndZ=0
    g22: LineSegment StartX=-0.8 StartY=52.8 StartZ=0 EndX=27 EndY=52.8 EndZ=0
    g23: LineSegment StartX=50 StartY=53 StartZ=0 EndX=50 EndY=52.8 EndZ=0
    g24: ArcOfCircle CenterX=50 CenterY=54.5 CenterZ=0 NormalX=0 NormalY=0 NormalZ=1 AngleXU=0 Radius=1.5 StartAngle=3.27532 EndAngle=4.71239
    g25: ArcOfCircle CenterX=-0.8 CenterY=49.8 CenterZ=0 NormalX=0 NormalY=0 NormalZ=1 AngleXU=0 Radius=3 StartAngle=1.5708 EndAngle=3.14159
  constraints (79):
    c: Coincident(g13,g12)
    c: Coincident(g13,g4)
    c: Coincident(g18,g16)
    c: Coincident(g17,g18)
    c: Coincident(g3,g5)
    c: Coincident(g3,g4)
    c: Coincident(g2,g25)
    c: Coincident(g2,g17)
    c: Coincident(g11,g12)
    c: Coincident(g1,g5)
    c: Coincident(g22,g25)
    c: Coincident(g16,g15)
    c: Coincident(g14,g22)
    c: Coincident(g15,g14)
    c: Coincident(g20,g21)
    c: Coincident(g19,g21)
    c: Coincident(g23,g24)
    c: Coincident(g10,g11)
    c: Coincident(g1,g6)
    c: Coincident(g0,g6)
    c: Coincident(g0,g7)
    c: Coincident(g9,g7)
    c: Coincident(g10,g8)
    c: Coincident(g9,g8)
    c: Radius(g25) = 3
    c: Equal(g6,g5)
    c: Equal(g5,g25)
    c: DistanceY(g-15,g22) = 3.8
    c: Vertical(g16,g22)
    c: Vertical(g22,g15)
    c: Horizontal(g16,g2)
    c: Horizontal(g2,g16)
    c: Vertical(g2)
    c: Horizontal(g17)
    c: Vertical(g18)
    c: Horizontal(g2,g-16)
    c: Coincident(g16,g25)
    c: DistanceX(g2,g-15) = 3.8
    c: Horizontal(g15)
    c: Horizontal(g22)
    c: Vertical(g14,g-9)
    c: Vertical(g-9,g14)
    c: DistanceY(g14,g14) = 1.5
    c: Vertical(g21)
    c: Horizontal(g20,g14)
    c: Horizontal(g19,g14)
    c: Horizontal(g19,g19)
    c: Horizontal(g20,g20)
    c: Coincident(g-12,g23)
    c: Vertical(g23)
    c: Coincident(g24,g-12)
    c: Coincident(g19,g24)
    c: Coincident(g20,g23)
    c: Vertical(g20,g-9)
    c: DistanceX(g3,g-1) = 3.8
    c: DistanceY(g1,g-1) = 3.8
    c: Coincident(g5,g12)
    c: Vertical(g1,g11)
    c: Vertical(g11,g5)
    c: Horizontal(g5,g3)
    c: Horizontal(g3,g12)
    c: Horizontal(g3,g4)
    c: Horizontal(g4,g-7)
    c: Vertical(g3)
    c: Vertical(g13)
    c: DistanceX(g4,g3) = 1.5
    c: Coincident(g6,g10)
    c: Vertical(g6,g1)
    c: Vertical(g1,g10)
    c: Horizontal(g8,g0)
    c: Horizontal(g0,g6)
    c: Horizontal(g1)
    c: Horizontal(g11)
    c: Vertical(g8)
    c: Vertical(g0)
    c: Coincident(g9,g-8)
    c: Coincident(g7,g-8)
    c: Horizontal(g7)
    c: DistanceX(g-14,g0) = 23.8
FEATURE [PartDesign::Pad] Pad006  label="dust_cover_pad"
  BaseFeature = -> Pad005
  Length = 4
  Length2 = 100
  Profile = -> Sketch007
  Type = 0
FEATURE [Sketcher::SketchObject] Sketch008  label="top edge trim"
  ExternalGeometry = -> [Pad006]
  MapMode = 5
  Placement = pos=(0,0,5) rot=(0,0,1;0rad)
  Support = -> [Pad006]
  sketch-geometry (7):
    g0: ArcOfCircle CenterX=83 CenterY=54.5 CenterZ=0 NormalX=0 NormalY=0 NormalZ=1 AngleXU=0 Radius=1.5 StartAngle=4.91375 EndAngle=6.28319
    g1: LineSegment StartX=84.5 StartY=54.5 StartZ=0 EndX=84.5 EndY=-8 EndZ=0
    g2: LineSegment StartX=84.5 StartY=-8 StartZ=0 EndX=30.5 EndY=-8 EndZ=0
    g3: ArcOfCircle CenterX=33.2 CenterY=-8 CenterZ=0 NormalX=0 NormalY=0 NormalZ=1 AngleXU=0 Radius=2.7 StartAngle=1.5708 EndAngle=3.14159
    g4: LineSegment StartX=83.3 StartY=-0.8 StartZ=0 EndX=83.3 EndY=53.0303 EndZ=0
    g5: ArcOfCircle CenterX=78.8 CenterY=-0.8 CenterZ=0 NormalX=0 NormalY=0 NormalZ=1 AngleXU=0 Radius=4.5 StartAngle=4.71239 EndAngle=6.28319
    g6: LineSegment StartX=33.2 StartY=-5.3 StartZ=0 EndX=78.8 EndY=-5.3 EndZ=0
  constraints (19):
    c: Vertical(g1)
    c: Horizontal(g2)
    c: Coincident(g2,g1)
    c: Coincident(g1,g0)
    c: Coincident(g2,g-3)
    c: Coincident(g3,g2)
    c: Coincident(g4,g0)
    c: Coincident(g3,g6)
    c: Coincident(g5,g4)
    c: Coincident(g0,g-4)
    c: Coincident(g0,g-6)
    c: Radius(g0) = 1.5
    c: Coincident(g4,g-5)
    c: Coincident(g5,g-5)
    c: Radius(g5) = 4.5
    c: Coincident(g6,g5)
    c: Horizontal(g6)
    c: Horizontal(g3,g2)
    c: Vertical(g3,g3)
FEATURE [PartDesign::Pocket] Pocket001  label="top edge trim pocket"
  BaseFeature = -> Pad006
  Length = 5
  Length2 = 100
  Profile = -> Sketch008
  Type = 0
FEATURE [Sketcher::SketchObject] Sketch009  label="belt clip guide"
  ExternalGeometry = -> [Pocket001]
  MapMode = 5
  Placement = pos=(0,0,5) rot=(0,0,1;0rad)
  Support = -> [Pocket001]
  sketch-geometry (8):
    g0: LineSegment StartX=63 StartY=20 StartZ=0 EndX=43 EndY=20 EndZ=0
    g1: LineSegment StartX=43 StartY=20 StartZ=0 EndX=43 EndY=10 EndZ=0
    g2: LineSegment StartX=43 StartY=10 StartZ=0 EndX=63 EndY=10 EndZ=0
    g3: LineSegment StartX=63 StartY=10 StartZ=0 EndX=63 EndY=20 EndZ=0
    g4: LineSegment StartX=63 StartY=39 StartZ=0 EndX=43 EndY=39 EndZ=0
    g5: LineSegment StartX=43 StartY=39 StartZ=0 EndX=43 EndY=29 EndZ=0
    g6: LineSegment StartX=43 StartY=29 StartZ=0 EndX=63 EndY=29 EndZ=0
    g7: LineSegment StartX=63 StartY=29 StartZ=0 EndX=63 EndY=39 EndZ=0
  constraints (24):
    c: Coincident(g1,g2)
    c: Coincident(g0,g1)
    c: Coincident(g5,g6)
    c: Coincident(g4,g5)
    c: Coincident(g2,g3)
    c: Coincident(g0,g3)
    c: Coincident(g6,g7)
    c: Coincident(g4,g7)
    c: Horizontal(g6)
    c: Horizontal(g4)
    c: Horizontal(g0)
    c: Horizontal(g2)
    c: Vertical(g3)
    c: Vertical(g7)
    c: Vertical(g5)
    c: Vertical(g1)
    c: Vertical(g0,g5)
    c: Vertical(g0,g6)
    c: DistanceY(g4,g-4) = 10
    c: DistanceY(g-5,g2) = 10
    c: DistanceY(g3,g3) = 10
    c: DistanceY(g7,g7) = 10
    c: DistanceX(g0,g0) = 20
    c: DistanceX(g-4,g4) = 5
FEATURE [PartDesign::Pocket] Pocket002  label="belt clip guide pocket"
  BaseFeature = -> Pocket001
  Length = 5
  Length2 = 100
  Profile = -> Sketch009
  Type = 0
FEATURE [PartDesign::Body] Body  label="raspberry holster v1.0"
  Group = -> [Sketch,Pad,Sketch001,Pad001,Sketch002,Pad002,Sketch003,Pocket,Sketch004,Pad003,Sketch005,Pad004,Sketch006,Pad005,Sketch007,Pad006,Sketch008,Pocket001,Sketch009,Pocket002]
  Origin = -> Origin
  Tip = -> Pocket002
